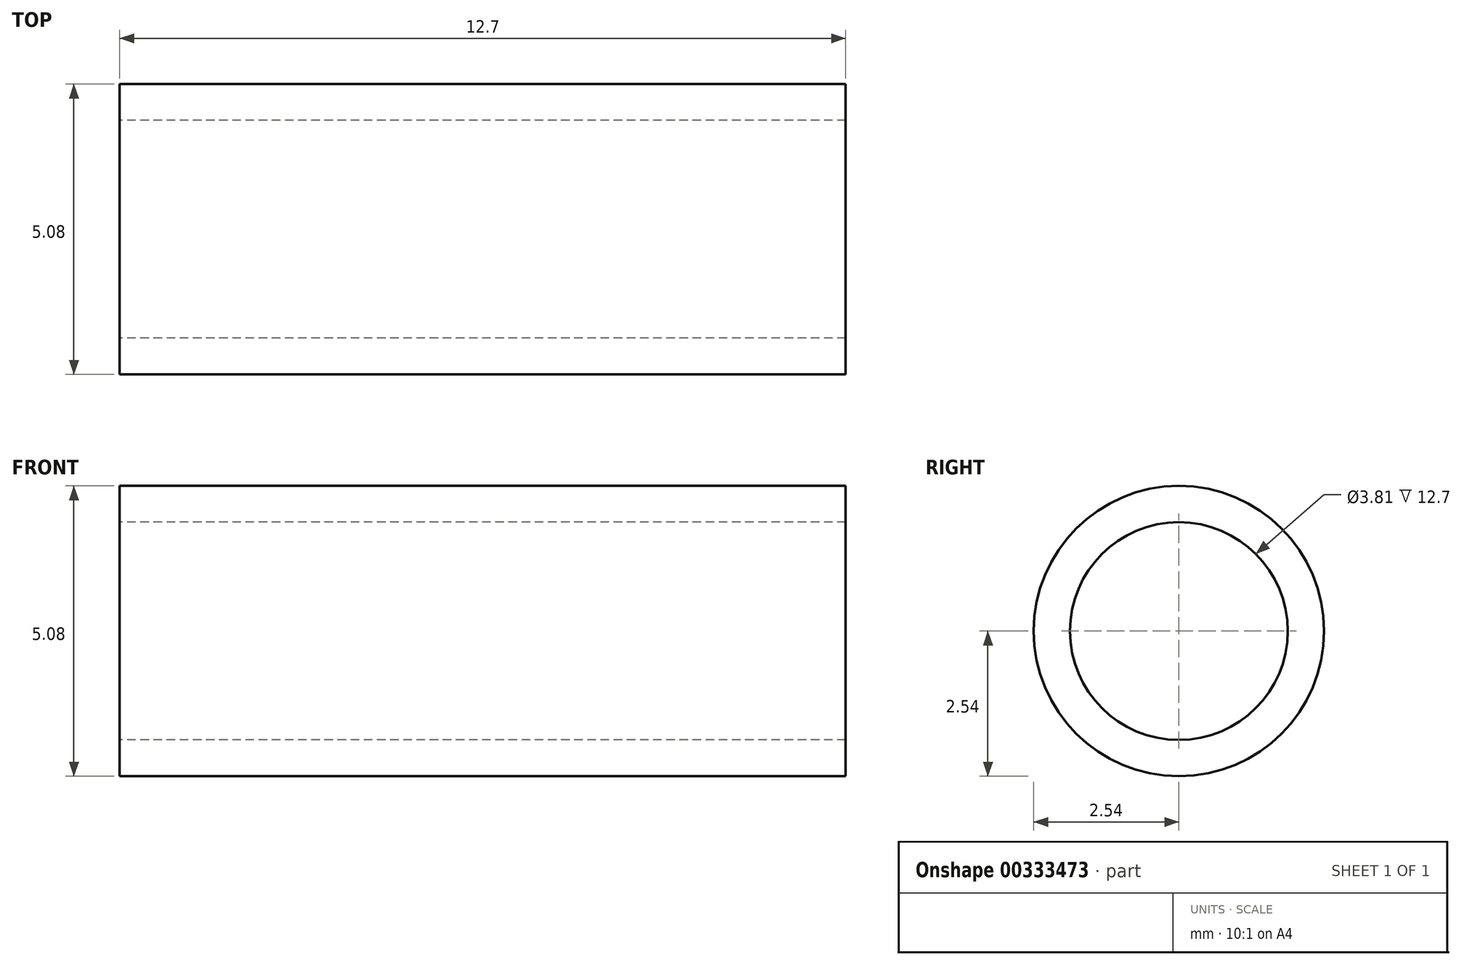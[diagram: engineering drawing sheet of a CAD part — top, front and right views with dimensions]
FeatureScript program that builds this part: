
annotation { "Feature Type Name" : "Feature", "Feature Type Description" : "" }
export const myFeature = defineFeature(function(context is Context, id is Id, definition is map)
    precondition{}
    {
        {
            var Q0;
            Q0=qCreatedBy(makeId("Right.planeOp"),FACE);
            var sketch = newSketch(context, id + "F0", { "sketchPlane" : qUnion([Q0])});
            skCircle(sketch, "E0", {"center": v(0, 0) * mm, "radius": 2.54 * mm});
            skCircle(sketch, "E1", {"center": v(0, 0) * mm, "radius": 1.9 * mm});
            skSolve(sketch);
        }
        {
            var Q0;
            Q0=makeQuery(id+"F0.imprint","IMPRINT",FACE,{"disambiguationData":[TD([[makeQuery(id+"F0.imprint","IMPRINT",EDGE,{"derivedFrom":sQuery(id+"F0.wireOp",EDGE,"E0")}),1.0]])]});
            extrude(context, id + "F1", {"entities" : qUnion([Q0]), "depth" : 12.7 * mm});
        }
    });
